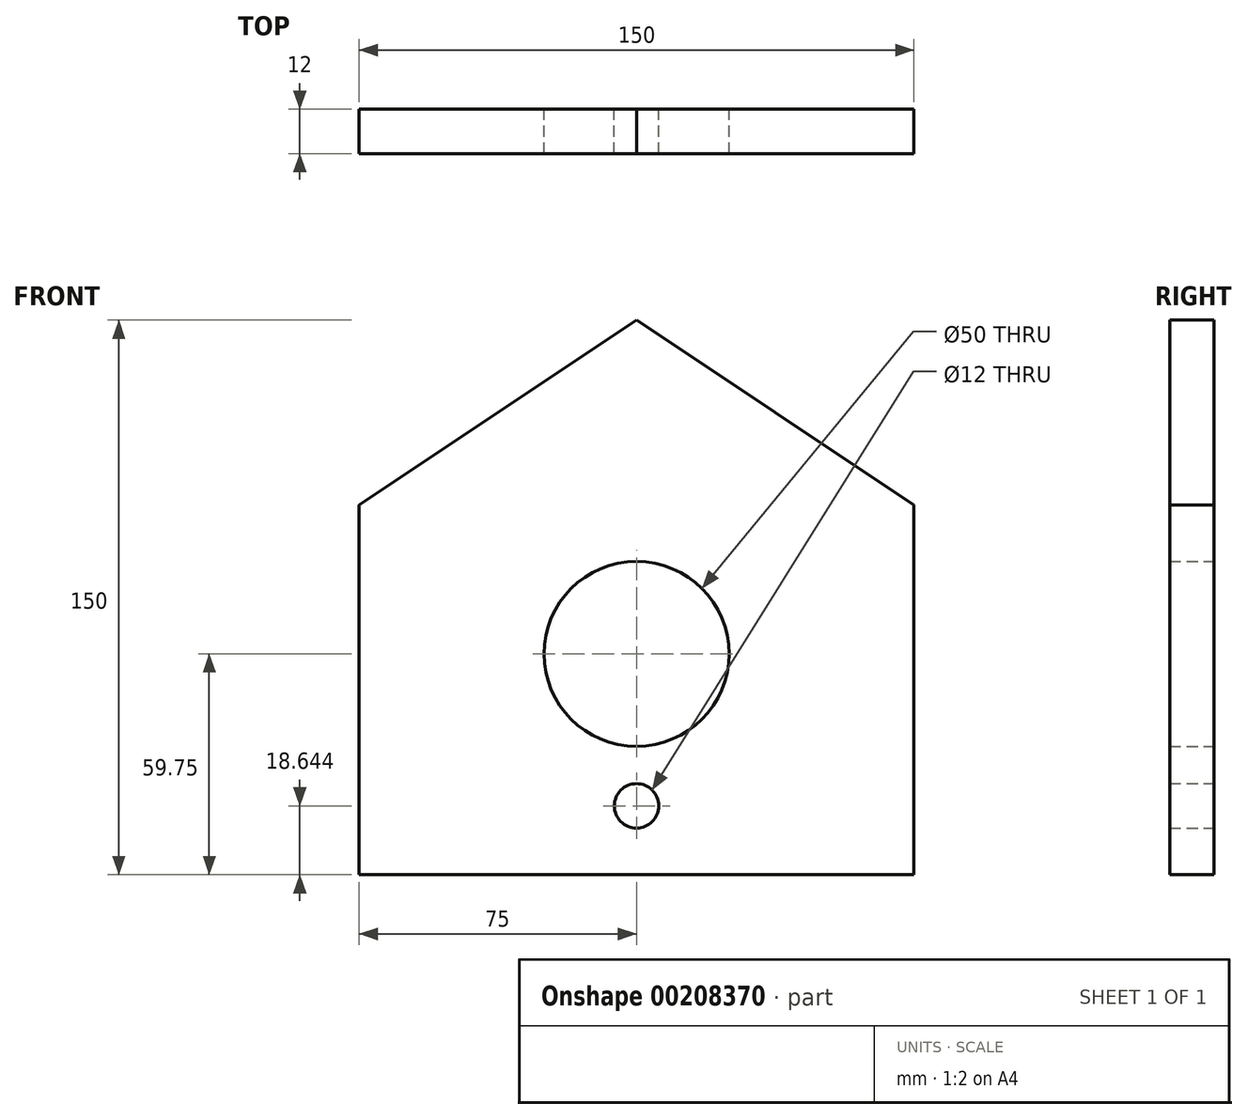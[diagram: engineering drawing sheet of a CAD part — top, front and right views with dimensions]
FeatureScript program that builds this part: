
annotation { "Feature Type Name" : "Feature", "Feature Type Description" : "" }
export const myFeature = defineFeature(function(context is Context, id is Id, definition is map)
    precondition{}
    {
        {
            var Q0;
            Q0=qCreatedBy(makeId("Front.planeOp"),FACE);
            var sketch = newSketch(context, id + "F0", { "sketchPlane" : qUnion([Q0])});
            skLineSegment(sketch, "E0.bottom", {"start": v(-75, 0) * mm, "end": v(75, 0) * mm});
            skLineSegment(sketch, "E0.left", {"start": v(-75, 0) * mm, "end": v(-75, 100) * mm});
            skLineSegment(sketch, "E0.right", {"start": v(75, 0) * mm, "end": v(75, 100) * mm});
            skLineSegment(sketch, "E1", {"start": v(-75, 100) * mm, "end": v(0, 150) * mm});
            skLineSegment(sketch, "E2", {"start": v(0, 150) * mm, "end": v(75, 100) * mm});
            skCircle(sketch, "E3", {"center": v(0, 59.75) * mm, "radius": 25 * mm});
            skCircle(sketch, "E4", {"center": v(0, 18.64) * mm, "radius": 6 * mm});
            skSolve(sketch);
        }
        {
            var Q0;
            Q0=makeQuery(id+"F0.imprint","IMPRINT",FACE,{"disambiguationData":[TD([[makeQuery(id+"F0.imprint","IMPRINT",EDGE,{"derivedFrom":sQuery(id+"F0.wireOp",EDGE,"E0.bottom")}),1.0]])]});
            extrude(context, id + "F1", {"entities" : qUnion([Q0]), "depth" : 12 * mm});
        }
    });
